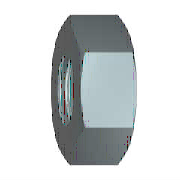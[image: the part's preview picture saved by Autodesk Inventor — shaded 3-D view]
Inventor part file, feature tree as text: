
AUTODESK INVENTOR PART (.ipt)
format: ipt  version: 2020 (Build 240168000, 168)  size: 164,864 bytes
history: native  units: mm (DEFAULTED — no unit token found)
features: sketch x3, other x2, extrude x1, hole x1, plane x1
ambient origin geometry x7: Origin, YZ Plane, XZ Plane, X Axis, Y Axis, Z Axis, Center Point
bodies: Solid1 (feature_tree)
feature tree (8):
  extrude  "Bryła"  Depth=6.350853mm
  other  "Faza1"
  hole  "Gwint"  [1 undecoded]
  other  "Work Axis1"
  plane  "Work Plane1"
  sketch  "Szkic1"
  sketch  "Szkic2"
  sketch  "Szkic3"
note: 1 required parameter value undecoded (feature->parameter linkage not recoverable at this tier; creation-order binding heuristic only, values carry confidence <= 0.55)
